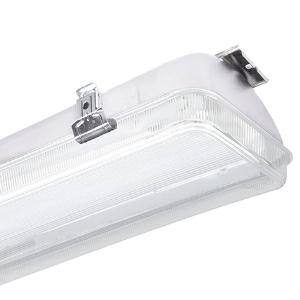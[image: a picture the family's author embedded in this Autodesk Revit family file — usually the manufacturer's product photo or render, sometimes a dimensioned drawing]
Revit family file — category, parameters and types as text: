
# Revit family: 3f_filippi_-_beta_235_75_pc_concentrato_3f_filippi_-_52524_-_beta_235_led_752x45_conc_l1265
name_source: partatom
category: Lighting Fixtures
units: mm (PartAtom-declared; Revit-internal decimal feet)

## family parameters
Cut with Voids When Loaded = No
Host = Face
Light Source = No
Part Type = Normal
Room Calculation Point = No
Round Connector Dimension = Use Diameter
Shared = No

## types (1)
- 3F Filippi - Beta 235 75 PC Concentrato (1 x LED, 13397 lm, 92 W, 4000 K)
    Apparent Load = 92 VA
    Approval mark = CE
    CIE Flux Codes = 71 90 98 98 100
    Color Rendering = 80
    Color Temperature = 4000 K
    Control Gear = Electronic ballast
    Default Elevation = 1800 mm
    Description = ILLUMINOTECHNICAL
Luminous efficiency 100% (DLOR 99%, ULOR 1%).
Initial luminous flux of the luminaire 13397 lm.
Concentrated elliptical distribution.
Installation Interdistance Transv.D = 0.64 x hu - Long.D = 1.03 x hu.
Tabular UGR (CIE 117 - 4H-8H; S=0.25H; 70/50/20): RUG 19.2 - 20.7.
Beam angle: 40° - 71°.
Luminous efficacy 146 lm/W.
Lifetime (L93/B10): 30000 h. (tq+25°C)
Lifetime (L90/B10): 50000 h. (tq+25°C)
Lifetime (L85/B10): 80000 h. (tq+25°C)
Lifetime (L80/B10): 100000 h. (tq+25°C)
Lifetime (L85/B10): 50000 h. (tq+45°C)
Sudden decreased luminous flux after 50000 hours: 0% (C0).
Photobiological safety in compliance with IEC/TR 62778: RG0 risk exempt, (IEC 62471).
In compliance with IEC/EN 62722-2-1 - IEC/EN 62717 standards.

SOURCE
2 linear LED modules 45W/840.
Energy efficiency class (UE 2019/2020 - UE 2019/2015): C.
CIE 13.3 Colour rendering index: CRI >80 (R9 <50%).
IES TM-30 Fidelity Index: Rf = 84 Rg = 95.
CCT nominal colour temperature 4000 K.
Colour initial tolerance (MacAdam): SDCM 3.

MECHANICAL
Single-piece housing in pressed steel, powder-coated in white epoxy-polyester.
Polycarbonate screen etched internally, V2 self-extinguishing, UV stabilised, injection moulded.
Ecologic anti-aging injected sealing gasket.
Oversized gear-tray reflector unit in highly reflective white painted hot-galvanised steel.
Methacrylate (PMMA) lenses with external flat surface.
Galvanised steel snap-lock clips for diffuser mounting (safety n° 4 per fixture).
Luminaire with limited surface temperature. - D - (EN 60598-2-24)
Dimensions: 1265x235 mm, height 135 mm. Weight 7.415 kg.
IP65 protection degree.
Mechanical strength to impacts IK10 (20 joule).
Glow-wire test resistance 850°C.

ELECTRICAL
Halogen Free electronic wiring 230V-50/60Hz, power factor 0.95, THD <25%, constant output current, class I, 1 driver.
Power of the luminaire 92 W.
ENEC - CE.
Flicker: <4%.
Luminaire compliant with EN 60598-2-22 for power supply from a centralised emergency system CPSS (Central Power Supply System), not incorporated in the luminaire - high risk areas excluded. The default power and flux are 100% in AC and 100% in DC.
Ambient temperature from -20°C to +45°C.
Temperature class T6 max 85°C.
Quick connection via M20 3P connector with 9-13 mm tightening range.
Relative humidity UR: <85%.

INSTALLATION
Ceiling / Suspended / Wall.
All accessories dedicated to this product are available on the Catalog and on our website www.3F-Filippi.com.

APPLICATIONS
Suitable product for food production plants (HACCP), IFS (Food Version 6), BRC (GSFS Food Version 7).
Dry, dusty indoor environments, subject to occasional water splashes.
Industrial environments, warehouses, environments where security locks are required on all clips, e.g. prisons (on request).
Environments in which it is necessary a total protection against falling fragments (eg environments with foodstuffs or machines with moving parts or with extreme temperature changes), use luminaires with laminated glass.
Tempered glass is not immune to falling fragments from harmless and caused by shocks or exceptionally derived from the tempering process.

WARNING
Fixture not suitable for cold stores with an ambient temperature <0°C and/or relative humidity >85%.
Luminaire designed for disposal/recycling at end-of-life.
Replaceable (LED only) light source by a professional. Replaceable control gear by a professional.
    Height = 135 mm
    Lamp = 1 x LED
    Lamp Light Flux = 13397 lm
    Lamp Power = 92 W
    Lamp count = 1
    Length = 1265 mm
    Lifetime = 50000 h
    Luminous efficacy = 146 lm/W
    Manufacturer = 3F Filippi
    ModVariant = No
    Model = 3F Filippi - 52524 - Beta 235 LED 752x45 CONC L1265
    Mounting Place = Ceiling
    Mounting Type = Pendant
    Number of Poles = 1
    OnlyDefault = Yes
    Power Factor = 1
    Product Name = 3F Filippi - Beta 235 75 PC Concentrato
    Product group = pendant luminaire
    ProductGroupID = 9
    Protection Class = Protection class I
    Protection Degree = IP 65
    RLX_Detail_Level = 1
    RLX_Emergency_Light_Flux = 0 lm
    RLX_Emergency_Type = 0
    RLX_Emergency_Type_DB = No
    RlxData = <blob elided: 89093 chars, md5=ea373e4f>
    Socket = socket
    Standby Power = 0 W
    System Light Flux = 13397 lm
    System Power = 92 W
    Type Comments = Product without accessories
    Type Image = 3ffilippi_beta_235_led_75_l655_l1265.jpg
    URL = http://relux.com
    VarID = ---
    Voltage = 0 V
    Weight = 0.00 kg
    Width = 235 mm

## geometry (parser evidence)
native form markers: Blend x4, Sweep x10
no freeform markers — native parametric forms only
